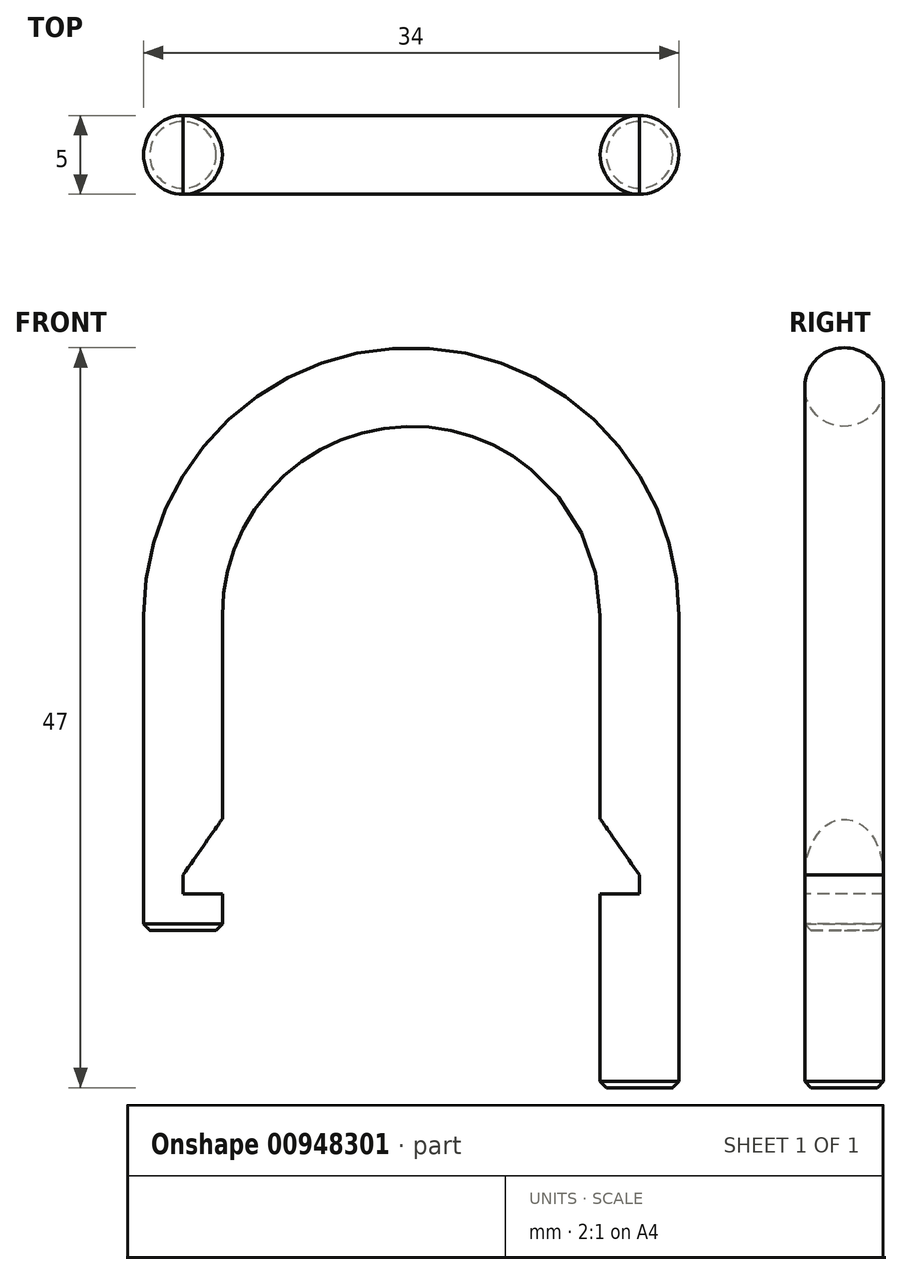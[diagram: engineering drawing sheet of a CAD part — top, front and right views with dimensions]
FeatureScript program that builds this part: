
annotation { "Feature Type Name" : "Feature", "Feature Type Description" : "" }
export const myFeature = defineFeature(function(context is Context, id is Id, definition is map)
    precondition{}
    {
        {
            var Q0;
            Q0=qCreatedBy(makeId("Top.planeOp"),FACE);
            var sketch = newSketch(context, id + "F0", { "sketchPlane" : qUnion([Q0])});
            skCircle(sketch, "E0", {"center": v(0, 0) * mm, "radius": 2.5 * mm});
            skSolve(sketch);
        }
        {
            var Q0;
            Q0=qCreatedBy(makeId("Front.planeOp"),FACE);
            var sketch = newSketch(context, id + "F1", { "sketchPlane" : qUnion([Q0])});
            skLineSegment(sketch, "E1", {"start": v(0, 0) * mm, "end": v(0, 30) * mm});
            skArc(sketch, "E2", {"start": v(0, 30) * mm, "mid": v(-14.5, 44.5) * mm, "end": v(-29, 30) * mm});
            skLineSegment(sketch, "E3", {"start": v(-29, 30) * mm, "end": v(-29, 10) * mm});
            skSolve(sketch);
        }
        {
            var Q0;
            Q0=makeQuery(id+"F0.imprint","IMPRINT",FACE,{"disambiguationData":[TD([[makeQuery(id+"F0.imprint","IMPRINT",EDGE,{"derivedFrom":sQuery(id+"F0.wireOp",EDGE,"E0")}),1.0]])]});
            var Q1;
            Q1=sQuery(id+"F1.wireOp",EDGE,"E1");
            var Q2;
            Q2=sQuery(id+"F1.wireOp",EDGE,"E2");
            var Q3;
            Q3=sQuery(id+"F1.wireOp",EDGE,"E3");
            sweep(context, id + "F2", {"profiles" : qUnion([Q0]), "path" : qUnion([Q1, Q2, Q3])});
        }
        {
            var Q0;
            Q0=qCreatedBy(makeId("Front.planeOp"),FACE);
            var sketch = newSketch(context, id + "F3", { "sketchPlane" : qUnion([Q0])});
            skLineSegment(sketch, "E4", {"start": v(0, 0) * mm, "end": v(-29, 0) * mm, "construction": true});
            skLineSegment(sketch, "E5", {"start": v(-29, 0) * mm, "end": v(-29, 12.3) * mm, "construction": true});
            skLineSegment(sketch, "E6", {"start": v(-29, 12.3) * mm, "end": v(-24.98, 12.3) * mm});
            skLineSegment(sketch, "E7", {"start": v(-24.98, 12.3) * mm, "end": v(-24.98, 19.23) * mm});
            skLineSegment(sketch, "E8", {"start": v(-24.98, 19.23) * mm, "end": v(-29, 13.5) * mm});
            skLineSegment(sketch, "E9", {"start": v(-29, 13.5) * mm, "end": v(-29, 12.3) * mm});
            skPoint(sketch, "E10", {"position": v(-14.5, 0) * mm});
            skLineSegment(sketch, "E11", {"start": v(-14.5, 0) * mm, "end": v(-14.5, 50.1) * mm, "construction": true});
            skLineSegment(sketch, "E12.MirrorCS", {"start": v(-4.02, 12.3) * mm, "end": v(-4.02, 19.23) * mm});
            skLineSegment(sketch, "E13.MirrorCS", {"start": v(-4.02, 19.23) * mm, "end": v(0, 13.5) * mm});
            skLineSegment(sketch, "E14.MirrorCS", {"start": v(0, 13.5) * mm, "end": v(0, 12.3) * mm});
            skLineSegment(sketch, "E15.MirrorCS", {"start": v(0, 12.3) * mm, "end": v(-4.02, 12.3) * mm});
            skSolve(sketch);
        }
        {
            var Q0;
            Q0=makeQuery(id+"F3.imprint","IMPRINT",FACE,{"disambiguationData":[TD([[makeQuery(id+"F3.imprint","IMPRINT",EDGE,{"derivedFrom":sQuery(id+"F3.wireOp",EDGE,"E6")}),1.0]])]});
            var Q1;
            Q1=makeQuery(id+"F3.imprint","IMPRINT",FACE,{"disambiguationData":[TD([[makeQuery(id+"F3.imprint","IMPRINT",EDGE,{"derivedFrom":sQuery(id+"F3.wireOp",EDGE,"E12.MirrorCS")}),-1.0]])]});
            extrude(context, id + "F4", {"entities" : qUnion([Q0, Q1]), "operationType" : NewBodyOperationType.REMOVE, "endBound" : BoundingType.THROUGH_ALL, "oppositeDirection" : true, "depth" : 25 * mm, "offsetDistance" : 25 * mm, "hasSecondDirection" : true, "secondDirectionBound" : SecondDirectionBoundingType.THROUGH_ALL, "secondDirectionOppositeDirection" : false, "secondDirectionDepth" : 25 * mm});
        }
        {
            var Q0;
            Q0=makeQuery(id+"F2.opSweep","CAP_FACE",FACE,{"disambiguationData":[OSD([sQuery(id+"F0.wireOp",EDGE,"E0"),sQuery(id+"F1.wireOp",VERTEX,"E3.end")])],"isStart":false});
            var Q1;
            Q1=makeQuery(id+"F2.opSweep","CAP_FACE",FACE,{"disambiguationData":[OSD([sQuery(id+"F0.wireOp",EDGE,"E0"),sQuery(id+"F1.wireOp",VERTEX,"E1.start")])],"isStart":true});
            chamfer(context, id + "F5", {"entities" : qUnion([Q0, Q1]), "width" : 0.39 * mm, "tangentPropagation" : true});
        }
    });
